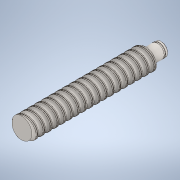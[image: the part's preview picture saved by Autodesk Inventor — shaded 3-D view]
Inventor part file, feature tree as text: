
AUTODESK INVENTOR PART (.ipt)
format: ipt  version: 2020.1 (Build 241239000, 239)  size: 2,407,936 bytes
history: native  units: mm
features: other x2, extrude x1, sketch x1
ambient origin geometry x8: Origin, YZ Plane, XZ Plane, XY Plane, X Axis, Y Axis, Z Axis, Center Point
bodies: Body1 (feature_tree)
feature tree (4):
  other  "Твердое тело1"
  extrude  "Выдавливание1"  Depth=300.0mm TaperAngle=0.0deg
  sketch  "Эскиз1"
  other  "Aesthetic Chamfer"
